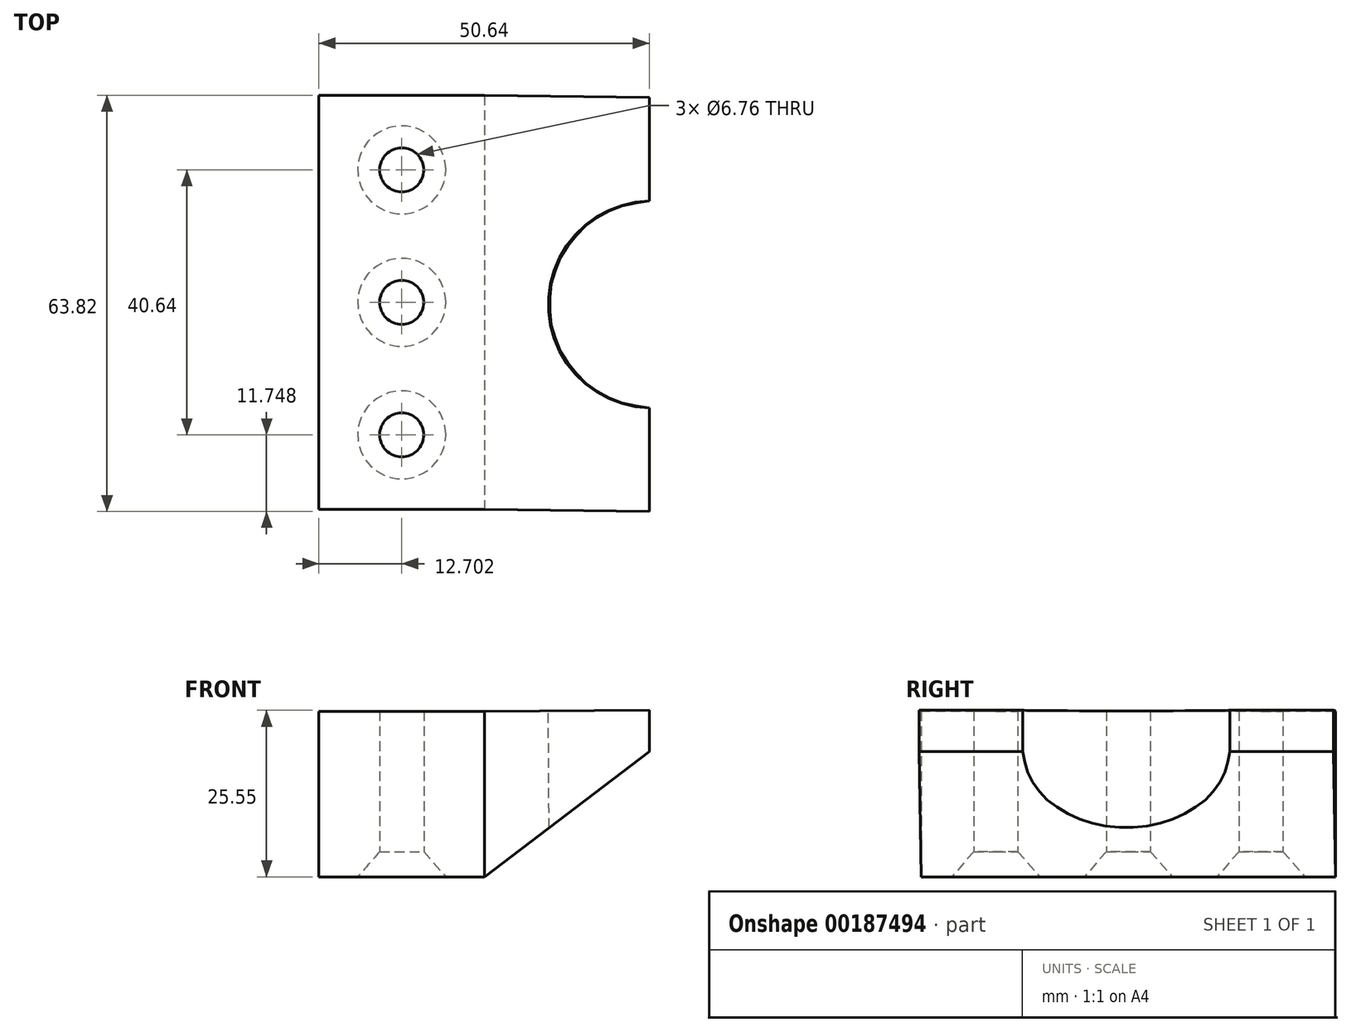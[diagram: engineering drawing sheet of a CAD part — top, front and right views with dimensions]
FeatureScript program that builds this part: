
annotation { "Feature Type Name" : "Feature", "Feature Type Description" : "" }
export const myFeature = defineFeature(function(context is Context, id is Id, definition is map)
    precondition{}
    {
        {
            var Q0;
            Q0=qCreatedBy(makeId("Top.planeOp"),FACE);
            var sketch = newSketch(context, id + "F0", { "sketchPlane" : qUnion([Q0])});
            skLineSegment(sketch, "E0.bottom", {"start": v(-25.24, 63.82) * mm, "end": v(0.16, 63.82) * mm});
            skLineSegment(sketch, "E0.top", {"start": v(-25.24, 0.32) * mm, "end": v(0.16, 0.32) * mm});
            skLineSegment(sketch, "E0.left", {"start": v(-25.24, 63.82) * mm, "end": v(-25.24, 0.32) * mm});
            skLineSegment(sketch, "E0.right", {"start": v(0.16, 63.82) * mm, "end": v(0.16, 0.32) * mm});
            skLineSegment(sketch, "E1", {"start": v(-12.54, 0.32) * mm, "end": v(-12.54, 11.75) * mm});
            skPoint(sketch, "E2", {"position": v(-12.54, 11.75) * mm});
            skLineSegment(sketch, "E3", {"start": v(-12.54, 11.75) * mm, "end": v(-12.54, 32.07) * mm});
            skPoint(sketch, "E3.endSnap0", {"position": v(0.16, 32.07) * mm});
            skLineSegment(sketch, "E4", {"start": v(-12.54, 32.07) * mm, "end": v(-12.54, 52.39) * mm});
            skPoint(sketch, "E4.endSnap0", {"position": v(-12.54, 21.9) * mm});
            skPoint(sketch, "E5", {"position": v(-12.54, 52.39) * mm});
            skPoint(sketch, "E6", {"position": v(-12.54, 32.07) * mm});
            skPoint(sketch, "E7", {"position": v(-94.86, 54.93) * mm});
            skSolve(sketch);
        }
        {
            var Q0;
            Q0 = qSketchRegion(id + "F0", true);
            extrude(context, id + "F1", {"entities" : qUnion([Q0]), "depth" : 25.4 * mm});
        }
        {
            var Q0;
            Q0=sQuery(id+"F0.wireOp",VERTEX,"E2");
            var Q1;
            Q1=sQuery(id+"F0.wireOp",VERTEX,"E6");
            var Q2;
            Q2=sQuery(id+"F0.wireOp",VERTEX,"E5");
            var Q3;
            Q3=makeQuery(id+"F1.opExtrude","SWEPT_BODY",BODY,{"disambiguationData":[OSD([sQuery(id+"F0.wireOp",EDGE,"E0.bottom"),sQuery(id+"F0.wireOp",EDGE,"E0.top"),sQuery(id+"F0.wireOp",EDGE,"E0.left"),sQuery(id+"F0.wireOp",EDGE,"E0.right")])]});
            hole(context, id + "F2", {"style" : HoleStyle.C_SINK, "endStyle" : HoleEndStyle.THROUGH, "oppositeDirection" : true, "standardTappedOrClearance" : lookupTablePath({ "standard" : "ANSI", "fit" : "Normal (ASME)", "size" : "1/4", "type" : "Clearance" }), "standardBlindInLast" : lookupTablePath({ "fit" : "Free", "standard" : "ANSI", "size" : "1/4", "type" : "Clearance" }), "holeDiameter" : 6.76 * mm, "cSinkDiameter" : 13.5 * mm, "cSinkAngle" : 82 * degree, "startFromSketch" : true, "locations" : qUnion([Q0, Q1, Q2]), "scope" : qUnion([Q3]), "isTappedThrough" : true});
        }
        {
            var Q0;
            Q0=qCreatedBy(makeId("Right.planeOp"),FACE);
            cPlane(context, id + "F3", {"entities" : qUnion([Q0]), "cplaneType" : CPlaneType.OFFSET, "offset" : 25.4 * mm, "width" : 152.4 * mm, "height" : 152.4 * mm});
        }
        {
            var Q0;
            Q0=qCreatedBy(id+"F3.planeOp",FACE);
            var sketch = newSketch(context, id + "F4", { "sketchPlane" : qUnion([Q0])});
            skLineSegment(sketch, "E8.bottom", {"start": v(0, 25.55) * mm, "end": v(63.5, 25.55) * mm});
            skLineSegment(sketch, "E8.top", {"start": v(0, 19.2) * mm, "end": v(63.5, 19.2) * mm});
            skLineSegment(sketch, "E8.left", {"start": v(0, 25.55) * mm, "end": v(0, 19.2) * mm});
            skLineSegment(sketch, "E8.right", {"start": v(63.5, 25.55) * mm, "end": v(63.5, 19.2) * mm});
            skSolve(sketch);
        }
        {
            var Q1;
            Q1=makeQuery(id+"F4.imprint","IMPRINT",FACE,{"disambiguationData":[TD([[makeQuery(id+"F4.imprint","IMPRINT",EDGE,{"derivedFrom":sQuery(id+"F4.wireOp",EDGE,"E8.bottom")}),-1.0]])]});
            var Q2;
            Q2=makeQuery(id+"F1.opExtrude","SWEPT_FACE",FACE,{"disambiguationData":[OSD([sQuery(id+"F0.wireOp",EDGE,"E0.right")])]});
            loft(context, id + "F5", {"operationType" : NewBodyOperationType.ADD, "sheetProfilesArray" : [{ "sheetProfileEntities" : qUnion([Q1]) }, { "sheetProfileEntities" : qUnion([Q2]) }]});
        }
        {
            var Q0;
            Q0=makeQuery(id+"F5.opLoft","SWEPT_FACE",FACE,{"disambiguationData":[OSD([sQuery(id+"F0.wireOp",EDGE,"E0.bottom"),sQuery(id+"F0.wireOp",EDGE,"E0.top"),sQuery(id+"F0.wireOp",EDGE,"E0.right"),sQuery(id+"F4.wireOp",EDGE,"E8.bottom"),sQuery(id+"F4.wireOp",EDGE,"E8.left"),sQuery(id+"F4.wireOp",EDGE,"E8.right")])]});
            var sketch = newSketch(context, id + "F6", { "sketchPlane" : qUnion([Q0])});
            skLineSegment(sketch, "E9", {"start": v(25.55, 0) * mm, "end": v(25.95, 31.75) * mm});
            skPoint(sketch, "E9.endSnap0", {"position": v(25.55, 31.75) * mm});
            skPoint(sketch, "E10", {"position": v(25.95, 31.75) * mm});
            skSolve(sketch);
        }
        {
            var Q0;
            Q0=sQuery(id+"F6.wireOp",VERTEX,"E9.end");
            var Q1;
            Q1=makeQuery(id+"F1.opExtrude","SWEPT_BODY",BODY,{"disambiguationData":[OSD([sQuery(id+"F0.wireOp",EDGE,"E0.bottom"),sQuery(id+"F0.wireOp",EDGE,"E0.top"),sQuery(id+"F0.wireOp",EDGE,"E0.left"),sQuery(id+"F0.wireOp",EDGE,"E0.right")])]});
            hole(context, id + "F7", {"style" : HoleStyle.SIMPLE, "endStyle" : HoleEndStyle.THROUGH, "holeDiameter" : 31.75 * mm, "startFromSketch" : true, "locations" : qUnion([Q0]), "scope" : qUnion([Q1]), "isTappedThrough" : true});
        }
    });
